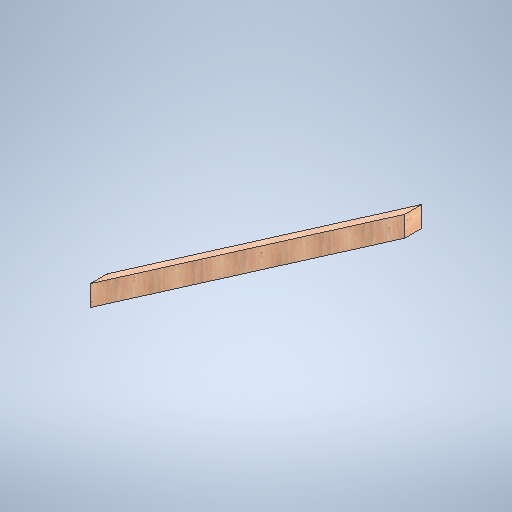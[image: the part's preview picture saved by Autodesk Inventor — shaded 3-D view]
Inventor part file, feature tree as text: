
AUTODESK INVENTOR PART (.ipt)
format: ipt  version: 2025 (Build 290162000, 162)  size: 272,384 bytes
history: native  units: in
note: dims shown in document units (in); Inventor stores cm internally (conversion verified against a paired STEP export)
features: extrude x1, sketch x1
ambient origin geometry x8: Origin, YZ Plane, XZ Plane, XY Plane, X Axis, Y Axis, Z Axis, Center Point
bodies: Solid1 (feature_tree)
feature tree (2):
  extrude  "Extrusion1"  Depth=4.0in TaperAngle=0.0deg
  sketch  "Sketch1"  dims[d2=4.0in d3=90.0deg d4=4.0in d5=0.0in]
